# Revit family: QF_Vollrath_CO4-208240HS_Conv Oven
name_source: partatom
category: Specialty Equipment
units: mm (PartAtom-declared; Revit-internal decimal feet)

## family parameters
Always vertical = Yes
Cut with Voids When Loaded = No
OmniClass Number = 23.40.40.00
OmniClass Title = Food Service Equipment and Furnishings
Part Type = Normal
Room Calculation Point = No
Round Connector Dimension = Use Diameter
Shared = No
Work Plane-Based = No

## types (1)
- QF_Vollrath_CO4-208240HS_Conv Oven
    Apparent Power = 2736 VA
    Conn Conduit = Yes
    Conn Plug = NEMA 6-15P
    Cycle = 0 Hz
    Default Elevation = 0 "
    Description = Convection Oven
    Elec Conn Connection Height = 0 "
    FL Amps = 11 A
    Foodservice Equipment Identifier = Yes
    Manufacturer = Vollrath
    Max Overcurrent Protection = 0 A
    Min Ckt Ampacity = 20 A
    Model = CO4-208240HS
    Phase = 0
    Volts = 240 V
    Watts = 2700 W
    Weight in Pounds = 0

## geometry (parser evidence)
native form markers: Sweep x2
no freeform markers — native parametric forms only
